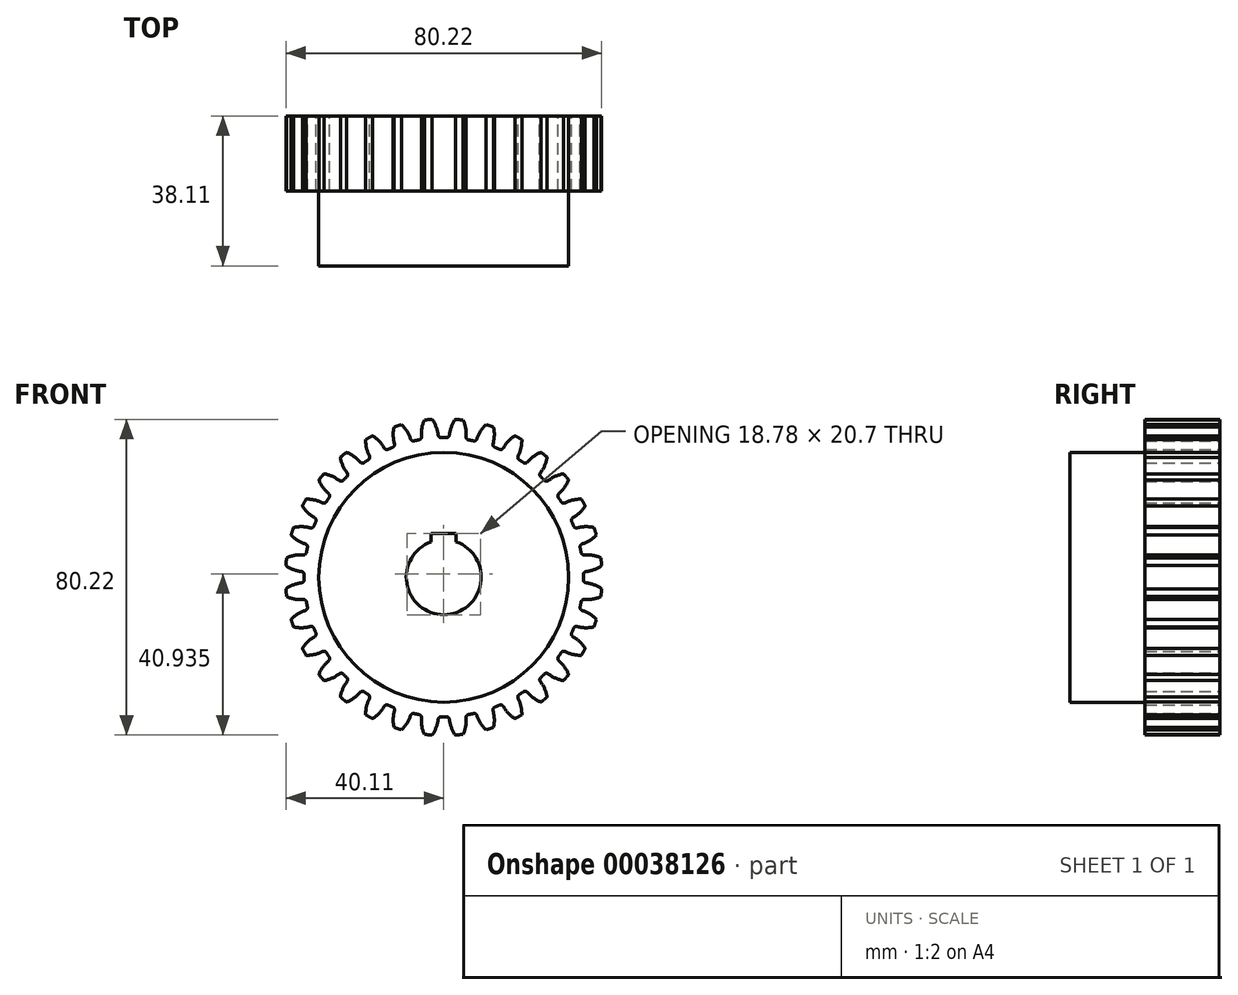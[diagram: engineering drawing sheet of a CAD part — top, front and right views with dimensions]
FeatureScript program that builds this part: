
annotation { "Feature Type Name" : "Feature", "Feature Type Description" : "" }
export const myFeature = defineFeature(function(context is Context, id is Id, definition is map)
    precondition{}
    {
        {
            var Q0;
            Q0=qCreatedBy(makeId("Front.planeOp"),FACE);
            var sketch = newSketch(context, id + "F0", { "sketchPlane" : qUnion([Q0])});
            skCircle(sketch, "E0", {"center": v(0, 0) * mm, "radius": 38.1 * mm});
            skCircle(sketch, "E1", {"center": v(0, 0) * mm, "radius": 40.22 * mm});
            skCircle(sketch, "E2", {"center": v(0, 0) * mm, "radius": 35.45 * mm});
            skSolve(sketch);
        }
        {
            var Q0;
            Q0 = qSketchRegion(id + "F0", true);
            var Q1;
            Q1=makeQuery(id+"F0.imprint","IMPRINT",FACE,{"disambiguationData":[TD([[makeQuery(id+"F0.imprint","IMPRINT",EDGE,{"derivedFrom":sQuery(id+"F0.wireOp",EDGE,"E2")}),1.0]])]});
            var Q2;
            Q2=makeQuery(id+"F0.imprint","IMPRINT",FACE,{"disambiguationData":[TD([[makeQuery(id+"F0.imprint","IMPRINT",EDGE,{"derivedFrom":sQuery(id+"F0.wireOp",EDGE,"E0")}),1.0]])]});
            extrude(context, id + "F1", {"entities" : qUnion([Q0, Q1, Q2]), "endBound" : BoundingType.SYMMETRIC, "depth" : 19.05 * mm});
        }
        {
            var Q0;
            Q0=qCreatedBy(makeId("Front.planeOp"),FACE);
            var sketch = newSketch(context, id + "F2", { "sketchPlane" : qUnion([Q0])});
            skLineSegment(sketch, "E3", {"start": v(0, 0) * mm, "end": v(0, 38.05) * mm, "construction": true});
            skLineSegment(sketch, "E4", {"start": v(0, 0) * mm, "end": v(-1.35, 35.43) * mm, "construction": true});
            skArc(sketch, "E5.0", {"start": v(3.48, 35.28) * mm, "mid": v(1.06, 35.44) * mm, "end": v(-1.35, 35.43) * mm});
            skArc(sketch, "E6.0", {"start": v(0.64, 35.45) * mm, "mid": v(0, 35.45) * mm, "end": v(-0.64, 35.45) * mm});
            skCircle(sketch, "E6.1", {"center": v(0, 0) * mm, "radius": 38.1 * mm, "construction": true});
            skArc(sketch, "E7.0", {"start": v(3.52, 40.83) * mm, "mid": v(0, 40.98) * mm, "end": v(-3.52, 40.83) * mm});
            skLineSegment(sketch, "E8", {"start": v(0, 0) * mm, "end": v(3.73, 37.87) * mm, "construction": true});
            skLineSegment(sketch, "E9", {"start": v(1.87, 38.05) * mm, "end": v(5.6, 37.69) * mm, "construction": true});
            skLineSegment(sketch, "E10", {"start": v(1.87, 38.05) * mm, "end": v(-1.87, 38.05) * mm, "construction": true});
            skArc(sketch, "E11", {"start": v(-1.4, 36.12) * mm, "mid": v(-2.1, 38.63) * mm, "end": v(-3.52, 40.83) * mm});
            skLineSegment(sketch, "E12", {"start": v(-1.87, 38.05) * mm, "end": v(0, 32.92) * mm, "construction": true});
            skArc(sketch, "E13.MirrorCS", {"start": v(1.4, 36.12) * mm, "mid": v(2.1, 38.63) * mm, "end": v(3.52, 40.83) * mm});
            skPoint(sketch, "E14.visualSharp", {"position": v(-1.35, 35.43) * mm});
            skArc(sketch, "E14.filletArc", {"start": v(-1.4, 36.12) * mm, "mid": v(-1.15, 35.64) * mm, "end": v(-0.64, 35.45) * mm});
            skPoint(sketch, "E15.newPointB", {"position": v(1.35, 35.43) * mm});
            skArc(sketch, "E15.filletArc", {"start": v(0.64, 35.45) * mm, "mid": v(1.15, 35.64) * mm, "end": v(1.4, 36.12) * mm});
            skSolve(sketch);
        }
        {
            var Q0;
            Q0 = qSketchRegion(id + "F2", true);
            extrude(context, id + "F3", {"entities" : qUnion([Q0]), "endBound" : BoundingType.SYMMETRIC, "depth" : 25.4 * mm});
        }
        {
            var Q0;
            Q0=makeQuery(id+"F3.opExtrude","SWEPT_BODY",BODY,{"disambiguationData":[OSD([sQuery(id+"F2.wireOp",EDGE,"E6.0"),sQuery(id+"F2.wireOp",EDGE,"E7.0"),sQuery(id+"F2.wireOp",EDGE,"E11"),sQuery(id+"F2.wireOp",EDGE,"E13.MirrorCS")])]});
            var Q1;
            Q1=sQuery(id+"F2.wireOp",EDGE,"E6.1");
            circularPattern(context, id + "F4", {"entities" : qUnion([Q0]), "axis" : qUnion([Q1]), "angle" : 360 * degree, "instanceCount" : 32, "equalSpace" : true});
        }
        {
            var Q0;
            Q0=makeQuery(id+"F4.opPattern","COPY",BODY,{"derivedFrom":makeQuery(id+"F3.opExtrude","SWEPT_BODY",BODY,{"disambiguationData":[OSD([sQuery(id+"F2.wireOp",EDGE,"E6.0"),sQuery(id+"F2.wireOp",EDGE,"E7.0"),sQuery(id+"F2.wireOp",EDGE,"E11"),sQuery(id+"F2.wireOp",EDGE,"E13.MirrorCS")])]}),"instanceName":"1"});
            var Q1;
            Q1=makeQuery(id+"F4.opPattern","COPY",BODY,{"derivedFrom":makeQuery(id+"F3.opExtrude","SWEPT_BODY",BODY,{"disambiguationData":[OSD([sQuery(id+"F2.wireOp",EDGE,"E6.0"),sQuery(id+"F2.wireOp",EDGE,"E7.0"),sQuery(id+"F2.wireOp",EDGE,"E11"),sQuery(id+"F2.wireOp",EDGE,"E13.MirrorCS")])]}),"instanceName":"2"});
            var Q2;
            Q2=makeQuery(id+"F4.opPattern","COPY",BODY,{"derivedFrom":makeQuery(id+"F3.opExtrude","SWEPT_BODY",BODY,{"disambiguationData":[OSD([sQuery(id+"F2.wireOp",EDGE,"E6.0"),sQuery(id+"F2.wireOp",EDGE,"E7.0"),sQuery(id+"F2.wireOp",EDGE,"E11"),sQuery(id+"F2.wireOp",EDGE,"E13.MirrorCS")])]}),"instanceName":"3"});
            var Q3;
            Q3=makeQuery(id+"F4.opPattern","COPY",BODY,{"derivedFrom":makeQuery(id+"F3.opExtrude","SWEPT_BODY",BODY,{"disambiguationData":[OSD([sQuery(id+"F2.wireOp",EDGE,"E6.0"),sQuery(id+"F2.wireOp",EDGE,"E7.0"),sQuery(id+"F2.wireOp",EDGE,"E11"),sQuery(id+"F2.wireOp",EDGE,"E13.MirrorCS")])]}),"instanceName":"4"});
            var Q4;
            Q4=makeQuery(id+"F4.opPattern","COPY",BODY,{"derivedFrom":makeQuery(id+"F3.opExtrude","SWEPT_BODY",BODY,{"disambiguationData":[OSD([sQuery(id+"F2.wireOp",EDGE,"E6.0"),sQuery(id+"F2.wireOp",EDGE,"E7.0"),sQuery(id+"F2.wireOp",EDGE,"E11"),sQuery(id+"F2.wireOp",EDGE,"E13.MirrorCS")])]}),"instanceName":"5"});
            var Q5;
            Q5=makeQuery(id+"F4.opPattern","COPY",BODY,{"derivedFrom":makeQuery(id+"F3.opExtrude","SWEPT_BODY",BODY,{"disambiguationData":[OSD([sQuery(id+"F2.wireOp",EDGE,"E6.0"),sQuery(id+"F2.wireOp",EDGE,"E7.0"),sQuery(id+"F2.wireOp",EDGE,"E11"),sQuery(id+"F2.wireOp",EDGE,"E13.MirrorCS")])]}),"instanceName":"6"});
            var Q6;
            Q6=makeQuery(id+"F4.opPattern","COPY",BODY,{"derivedFrom":makeQuery(id+"F3.opExtrude","SWEPT_BODY",BODY,{"disambiguationData":[OSD([sQuery(id+"F2.wireOp",EDGE,"E6.0"),sQuery(id+"F2.wireOp",EDGE,"E7.0"),sQuery(id+"F2.wireOp",EDGE,"E11"),sQuery(id+"F2.wireOp",EDGE,"E13.MirrorCS")])]}),"instanceName":"7"});
            var Q7;
            Q7=makeQuery(id+"F4.opPattern","COPY",BODY,{"derivedFrom":makeQuery(id+"F3.opExtrude","SWEPT_BODY",BODY,{"disambiguationData":[OSD([sQuery(id+"F2.wireOp",EDGE,"E6.0"),sQuery(id+"F2.wireOp",EDGE,"E7.0"),sQuery(id+"F2.wireOp",EDGE,"E11"),sQuery(id+"F2.wireOp",EDGE,"E13.MirrorCS")])]}),"instanceName":"8"});
            var Q8;
            Q8=makeQuery(id+"F4.opPattern","COPY",BODY,{"derivedFrom":makeQuery(id+"F3.opExtrude","SWEPT_BODY",BODY,{"disambiguationData":[OSD([sQuery(id+"F2.wireOp",EDGE,"E6.0"),sQuery(id+"F2.wireOp",EDGE,"E7.0"),sQuery(id+"F2.wireOp",EDGE,"E11"),sQuery(id+"F2.wireOp",EDGE,"E13.MirrorCS")])]}),"instanceName":"9"});
            var Q9;
            Q9=makeQuery(id+"F4.opPattern","COPY",BODY,{"derivedFrom":makeQuery(id+"F3.opExtrude","SWEPT_BODY",BODY,{"disambiguationData":[OSD([sQuery(id+"F2.wireOp",EDGE,"E6.0"),sQuery(id+"F2.wireOp",EDGE,"E7.0"),sQuery(id+"F2.wireOp",EDGE,"E11"),sQuery(id+"F2.wireOp",EDGE,"E13.MirrorCS")])]}),"instanceName":"10"});
            var Q10;
            Q10=makeQuery(id+"F4.opPattern","COPY",BODY,{"derivedFrom":makeQuery(id+"F3.opExtrude","SWEPT_BODY",BODY,{"disambiguationData":[OSD([sQuery(id+"F2.wireOp",EDGE,"E6.0"),sQuery(id+"F2.wireOp",EDGE,"E7.0"),sQuery(id+"F2.wireOp",EDGE,"E11"),sQuery(id+"F2.wireOp",EDGE,"E13.MirrorCS")])]}),"instanceName":"11"});
            var Q11;
            Q11=makeQuery(id+"F4.opPattern","COPY",BODY,{"derivedFrom":makeQuery(id+"F3.opExtrude","SWEPT_BODY",BODY,{"disambiguationData":[OSD([sQuery(id+"F2.wireOp",EDGE,"E6.0"),sQuery(id+"F2.wireOp",EDGE,"E7.0"),sQuery(id+"F2.wireOp",EDGE,"E11"),sQuery(id+"F2.wireOp",EDGE,"E13.MirrorCS")])]}),"instanceName":"12"});
            var Q12;
            Q12=makeQuery(id+"F4.opPattern","COPY",BODY,{"derivedFrom":makeQuery(id+"F3.opExtrude","SWEPT_BODY",BODY,{"disambiguationData":[OSD([sQuery(id+"F2.wireOp",EDGE,"E6.0"),sQuery(id+"F2.wireOp",EDGE,"E7.0"),sQuery(id+"F2.wireOp",EDGE,"E11"),sQuery(id+"F2.wireOp",EDGE,"E13.MirrorCS")])]}),"instanceName":"13"});
            var Q13;
            Q13=makeQuery(id+"F4.opPattern","COPY",BODY,{"derivedFrom":makeQuery(id+"F3.opExtrude","SWEPT_BODY",BODY,{"disambiguationData":[OSD([sQuery(id+"F2.wireOp",EDGE,"E6.0"),sQuery(id+"F2.wireOp",EDGE,"E7.0"),sQuery(id+"F2.wireOp",EDGE,"E11"),sQuery(id+"F2.wireOp",EDGE,"E13.MirrorCS")])]}),"instanceName":"14"});
            var Q14;
            Q14=makeQuery(id+"F4.opPattern","COPY",BODY,{"derivedFrom":makeQuery(id+"F3.opExtrude","SWEPT_BODY",BODY,{"disambiguationData":[OSD([sQuery(id+"F2.wireOp",EDGE,"E6.0"),sQuery(id+"F2.wireOp",EDGE,"E7.0"),sQuery(id+"F2.wireOp",EDGE,"E11"),sQuery(id+"F2.wireOp",EDGE,"E13.MirrorCS")])]}),"instanceName":"15"});
            var Q15;
            Q15=makeQuery(id+"F4.opPattern","COPY",BODY,{"derivedFrom":makeQuery(id+"F3.opExtrude","SWEPT_BODY",BODY,{"disambiguationData":[OSD([sQuery(id+"F2.wireOp",EDGE,"E6.0"),sQuery(id+"F2.wireOp",EDGE,"E7.0"),sQuery(id+"F2.wireOp",EDGE,"E11"),sQuery(id+"F2.wireOp",EDGE,"E13.MirrorCS")])]}),"instanceName":"16"});
            var Q16;
            Q16=makeQuery(id+"F4.opPattern","COPY",BODY,{"derivedFrom":makeQuery(id+"F3.opExtrude","SWEPT_BODY",BODY,{"disambiguationData":[OSD([sQuery(id+"F2.wireOp",EDGE,"E6.0"),sQuery(id+"F2.wireOp",EDGE,"E7.0"),sQuery(id+"F2.wireOp",EDGE,"E11"),sQuery(id+"F2.wireOp",EDGE,"E13.MirrorCS")])]}),"instanceName":"17"});
            var Q17;
            Q17=makeQuery(id+"F4.opPattern","COPY",BODY,{"derivedFrom":makeQuery(id+"F3.opExtrude","SWEPT_BODY",BODY,{"disambiguationData":[OSD([sQuery(id+"F2.wireOp",EDGE,"E6.0"),sQuery(id+"F2.wireOp",EDGE,"E7.0"),sQuery(id+"F2.wireOp",EDGE,"E11"),sQuery(id+"F2.wireOp",EDGE,"E13.MirrorCS")])]}),"instanceName":"18"});
            var Q18;
            Q18=makeQuery(id+"F4.opPattern","COPY",BODY,{"derivedFrom":makeQuery(id+"F3.opExtrude","SWEPT_BODY",BODY,{"disambiguationData":[OSD([sQuery(id+"F2.wireOp",EDGE,"E6.0"),sQuery(id+"F2.wireOp",EDGE,"E7.0"),sQuery(id+"F2.wireOp",EDGE,"E11"),sQuery(id+"F2.wireOp",EDGE,"E13.MirrorCS")])]}),"instanceName":"19"});
            var Q19;
            Q19=makeQuery(id+"F4.opPattern","COPY",BODY,{"derivedFrom":makeQuery(id+"F3.opExtrude","SWEPT_BODY",BODY,{"disambiguationData":[OSD([sQuery(id+"F2.wireOp",EDGE,"E6.0"),sQuery(id+"F2.wireOp",EDGE,"E7.0"),sQuery(id+"F2.wireOp",EDGE,"E11"),sQuery(id+"F2.wireOp",EDGE,"E13.MirrorCS")])]}),"instanceName":"20"});
            var Q20;
            Q20=makeQuery(id+"F4.opPattern","COPY",BODY,{"derivedFrom":makeQuery(id+"F3.opExtrude","SWEPT_BODY",BODY,{"disambiguationData":[OSD([sQuery(id+"F2.wireOp",EDGE,"E6.0"),sQuery(id+"F2.wireOp",EDGE,"E7.0"),sQuery(id+"F2.wireOp",EDGE,"E11"),sQuery(id+"F2.wireOp",EDGE,"E13.MirrorCS")])]}),"instanceName":"21"});
            var Q21;
            Q21=makeQuery(id+"F4.opPattern","COPY",BODY,{"derivedFrom":makeQuery(id+"F3.opExtrude","SWEPT_BODY",BODY,{"disambiguationData":[OSD([sQuery(id+"F2.wireOp",EDGE,"E6.0"),sQuery(id+"F2.wireOp",EDGE,"E7.0"),sQuery(id+"F2.wireOp",EDGE,"E11"),sQuery(id+"F2.wireOp",EDGE,"E13.MirrorCS")])]}),"instanceName":"22"});
            var Q22;
            Q22=makeQuery(id+"F4.opPattern","COPY",BODY,{"derivedFrom":makeQuery(id+"F3.opExtrude","SWEPT_BODY",BODY,{"disambiguationData":[OSD([sQuery(id+"F2.wireOp",EDGE,"E6.0"),sQuery(id+"F2.wireOp",EDGE,"E7.0"),sQuery(id+"F2.wireOp",EDGE,"E11"),sQuery(id+"F2.wireOp",EDGE,"E13.MirrorCS")])]}),"instanceName":"23"});
            var Q23;
            Q23=makeQuery(id+"F4.opPattern","COPY",BODY,{"derivedFrom":makeQuery(id+"F3.opExtrude","SWEPT_BODY",BODY,{"disambiguationData":[OSD([sQuery(id+"F2.wireOp",EDGE,"E6.0"),sQuery(id+"F2.wireOp",EDGE,"E7.0"),sQuery(id+"F2.wireOp",EDGE,"E11"),sQuery(id+"F2.wireOp",EDGE,"E13.MirrorCS")])]}),"instanceName":"24"});
            var Q24;
            Q24=makeQuery(id+"F4.opPattern","COPY",BODY,{"derivedFrom":makeQuery(id+"F3.opExtrude","SWEPT_BODY",BODY,{"disambiguationData":[OSD([sQuery(id+"F2.wireOp",EDGE,"E6.0"),sQuery(id+"F2.wireOp",EDGE,"E7.0"),sQuery(id+"F2.wireOp",EDGE,"E11"),sQuery(id+"F2.wireOp",EDGE,"E13.MirrorCS")])]}),"instanceName":"25"});
            var Q25;
            Q25=makeQuery(id+"F4.opPattern","COPY",BODY,{"derivedFrom":makeQuery(id+"F3.opExtrude","SWEPT_BODY",BODY,{"disambiguationData":[OSD([sQuery(id+"F2.wireOp",EDGE,"E6.0"),sQuery(id+"F2.wireOp",EDGE,"E7.0"),sQuery(id+"F2.wireOp",EDGE,"E11"),sQuery(id+"F2.wireOp",EDGE,"E13.MirrorCS")])]}),"instanceName":"26"});
            var Q26;
            Q26=makeQuery(id+"F4.opPattern","COPY",BODY,{"derivedFrom":makeQuery(id+"F3.opExtrude","SWEPT_BODY",BODY,{"disambiguationData":[OSD([sQuery(id+"F2.wireOp",EDGE,"E6.0"),sQuery(id+"F2.wireOp",EDGE,"E7.0"),sQuery(id+"F2.wireOp",EDGE,"E11"),sQuery(id+"F2.wireOp",EDGE,"E13.MirrorCS")])]}),"instanceName":"27"});
            var Q27;
            Q27=makeQuery(id+"F4.opPattern","COPY",BODY,{"derivedFrom":makeQuery(id+"F3.opExtrude","SWEPT_BODY",BODY,{"disambiguationData":[OSD([sQuery(id+"F2.wireOp",EDGE,"E6.0"),sQuery(id+"F2.wireOp",EDGE,"E7.0"),sQuery(id+"F2.wireOp",EDGE,"E11"),sQuery(id+"F2.wireOp",EDGE,"E13.MirrorCS")])]}),"instanceName":"28"});
            var Q28;
            Q28=makeQuery(id+"F4.opPattern","COPY",BODY,{"derivedFrom":makeQuery(id+"F3.opExtrude","SWEPT_BODY",BODY,{"disambiguationData":[OSD([sQuery(id+"F2.wireOp",EDGE,"E6.0"),sQuery(id+"F2.wireOp",EDGE,"E7.0"),sQuery(id+"F2.wireOp",EDGE,"E11"),sQuery(id+"F2.wireOp",EDGE,"E13.MirrorCS")])]}),"instanceName":"29"});
            var Q29;
            Q29=makeQuery(id+"F4.opPattern","COPY",BODY,{"derivedFrom":makeQuery(id+"F3.opExtrude","SWEPT_BODY",BODY,{"disambiguationData":[OSD([sQuery(id+"F2.wireOp",EDGE,"E6.0"),sQuery(id+"F2.wireOp",EDGE,"E7.0"),sQuery(id+"F2.wireOp",EDGE,"E11"),sQuery(id+"F2.wireOp",EDGE,"E13.MirrorCS")])]}),"instanceName":"30"});
            var Q30;
            Q30=makeQuery(id+"F4.opPattern","COPY",BODY,{"derivedFrom":makeQuery(id+"F3.opExtrude","SWEPT_BODY",BODY,{"disambiguationData":[OSD([sQuery(id+"F2.wireOp",EDGE,"E6.0"),sQuery(id+"F2.wireOp",EDGE,"E7.0"),sQuery(id+"F2.wireOp",EDGE,"E11"),sQuery(id+"F2.wireOp",EDGE,"E13.MirrorCS")])]}),"instanceName":"31"});
            var Q31;
            Q31=makeQuery(id+"F3.opExtrude","SWEPT_BODY",BODY,{"disambiguationData":[OSD([sQuery(id+"F2.wireOp",EDGE,"E6.0"),sQuery(id+"F2.wireOp",EDGE,"E7.0"),sQuery(id+"F2.wireOp",EDGE,"E11"),sQuery(id+"F2.wireOp",EDGE,"E13.MirrorCS")])]});
            var Q32;
            Q32=makeQuery(id+"F1.opExtrude","SWEPT_BODY",BODY,{"disambiguationData":[OSD([sQuery(id+"F0.wireOp",EDGE,"E1")])]});
            booleanBodies(context, id + "F5", {"operationType" : BooleanOperationType.SUBTRACTION, "tools" : qUnion([Q0, Q1, Q2, Q3, Q4, Q5, Q6, Q7, Q8, Q9, Q10, Q11, Q12, Q13, Q14, Q15, Q16, Q17, Q18, Q19, Q20, Q21, Q22, Q23, Q24, Q25, Q26, Q27, Q28, Q29, Q30, Q31]), "targets" : qUnion([Q32])});
        }
        {
            var Q0;
            Q0=makeQuery(id+"F1.opExtrude","CAP_FACE",FACE,{"disambiguationData":[OSD([sQuery(id+"F0.wireOp",EDGE,"E1")])],"isStart":false});
            var sketch = newSketch(context, id + "F6", { "sketchPlane" : qUnion([Q0])});
            skCircle(sketch, "E16", {"center": v(0, 0) * mm, "radius": 31.75 * mm});
            skSolve(sketch);
        }
        {
            var Q0;
            Q0 = qSketchRegion(id + "F6", true);
            extrude(context, id + "F7", {"entities" : qUnion([Q0]), "operationType" : NewBodyOperationType.ADD, "depth" : 19.05 * mm});
        }
        {
            var Q0;
            Q0=makeQuery(id+"F7.opExtrude","CAP_FACE",FACE,{"disambiguationData":[OSD([sQuery(id+"F6.wireOp",EDGE,"E16")])],"isStart":false});
            var sketch = newSketch(context, id + "F8", { "sketchPlane" : qUnion([Q0])});
            skArc(sketch, "E17", {"start": v(-3.18, 8.98) * mm, "mid": v(0, -9.53) * mm, "end": v(3.17, 8.98) * mm});
            skLineSegment(sketch, "E18.bottom", {"start": v(-3.17, 11.18) * mm, "end": v(3.18, 11.18) * mm});
            skLineSegment(sketch, "E18.left", {"start": v(-3.17, 11.18) * mm, "end": v(-3.17, 8.98) * mm});
            skLineSegment(sketch, "E18.right", {"start": v(3.18, 11.18) * mm, "end": v(3.18, 8.98) * mm});
            skLineSegment(sketch, "E19", {"start": v(0, 17.13) * mm, "end": v(0, -1.57) * mm, "construction": true});
            skSolve(sketch);
        }
        {
            var Q0;
            Q0=makeQuery(id+"F8.imprint","IMPRINT",FACE,{"disambiguationData":[TD([[makeQuery(id+"F8.imprint","IMPRINT",EDGE,{"derivedFrom":sQuery(id+"F8.wireOp",EDGE,"E17")}),1.0]])]});
            extrude(context, id + "F9", {"entities" : qUnion([Q0]), "operationType" : NewBodyOperationType.REMOVE, "endBound" : BoundingType.THROUGH_ALL, "oppositeDirection" : true, "depth" : 25.4 * mm});
        }
    });
